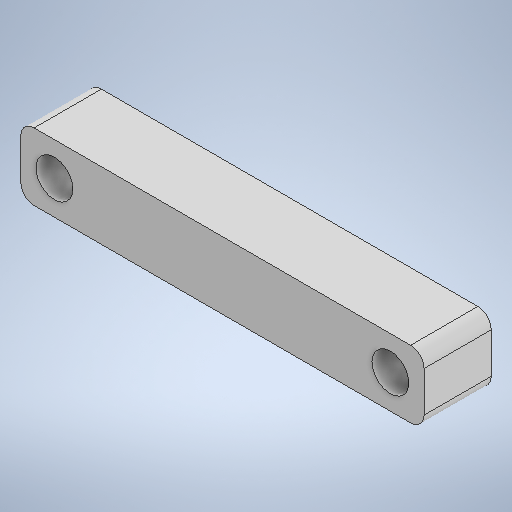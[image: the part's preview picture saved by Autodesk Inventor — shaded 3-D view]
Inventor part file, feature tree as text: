
AUTODESK INVENTOR PART (.ipt)
format: ipt  version: 2025.2 (Build 292293000, 293)  size: 240,128 bytes
history: native  units: mm
features: sketch x2, other x1, extrude x1, hole x1, mirror x1, fillet x1
ambient origin geometry x8: Origin, YZ Plane, XZ Plane, XY Plane, X Axis, Y Axis, Z Axis, Center Point
bodies: Body1 (feature_tree)
feature tree (7):
  other  "Bryła1"
  extrude  "Wyciągnięcie proste1"  Depth=60.0mm
  hole  "Otwór1"  [1 undecoded]
  mirror  "Odbij1"
  fillet  "Zaokrąglenie1"  Radius=10.0mm
  sketch  "Szkic1"
  sketch  "Szkic2"
note: 1 required parameter value undecoded (feature->parameter linkage not recoverable at this tier; creation-order binding heuristic only, values carry confidence <= 0.55)
